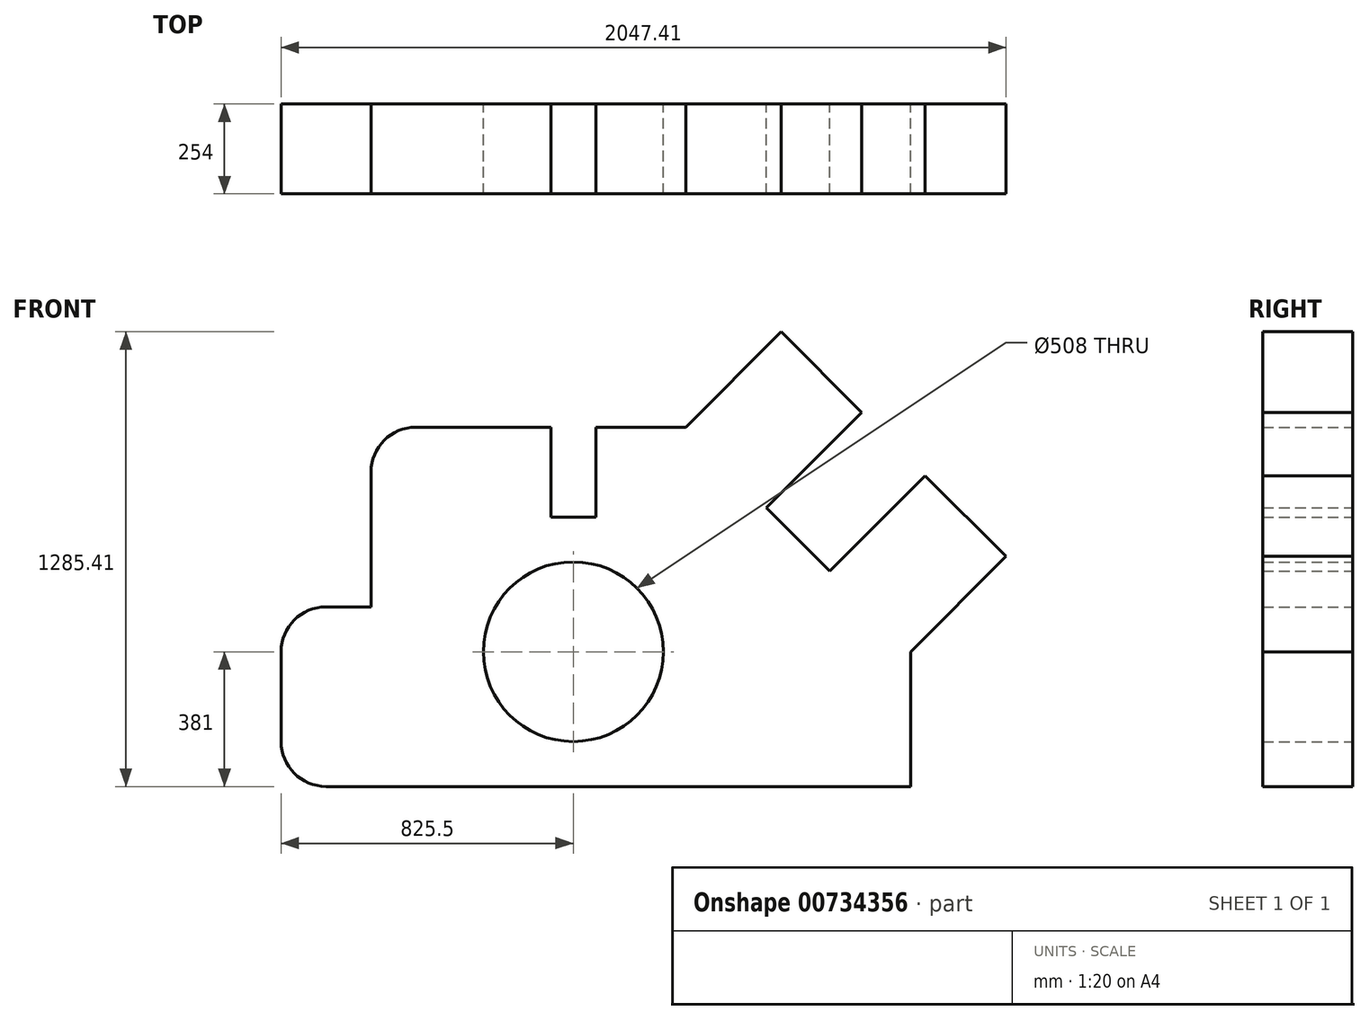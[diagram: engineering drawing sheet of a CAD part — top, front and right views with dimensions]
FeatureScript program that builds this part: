
annotation { "Feature Type Name" : "Feature", "Feature Type Description" : "" }
export const myFeature = defineFeature(function(context is Context, id is Id, definition is map)
    precondition{}
    {
        {
            var Q0;
            Q0=qCreatedBy(makeId("Front.planeOp"),FACE);
            var sketch = newSketch(context, id + "F0", { "sketchPlane" : qUnion([Q0])});
            skLineSegment(sketch, "E0", {"start": v(0, 127) * mm, "end": v(0, 381) * mm});
            skLineSegment(sketch, "E1", {"start": v(127, 0) * mm, "end": v(1778, 0) * mm});
            skLineSegment(sketch, "E2", {"start": v(1778, 0) * mm, "end": v(1778, 381) * mm});
            skLineSegment(sketch, "E3", {"start": v(1778, 381) * mm, "end": v(2047.4, 650.4) * mm});
            skLineSegment(sketch, "E4", {"start": v(127, 508) * mm, "end": v(254, 508) * mm});
            skLineSegment(sketch, "E5", {"start": v(254, 508) * mm, "end": v(254, 889) * mm});
            skLineSegment(sketch, "E6", {"start": v(381, 1016) * mm, "end": v(762, 1016) * mm});
            skLineSegment(sketch, "E7", {"start": v(762, 1016) * mm, "end": v(762, 762) * mm});
            skLineSegment(sketch, "E8", {"start": v(762, 762) * mm, "end": v(889, 762) * mm});
            skLineSegment(sketch, "E9", {"start": v(889, 762) * mm, "end": v(889, 1016) * mm});
            skLineSegment(sketch, "E10", {"start": v(889, 1016) * mm, "end": v(1143, 1016) * mm});
            skLineSegment(sketch, "E11", {"start": v(1143, 1016) * mm, "end": v(1412.4, 1285.4) * mm});
            skLineSegment(sketch, "E12", {"start": v(1412.4, 1285.4) * mm, "end": v(1639.92, 1057.9) * mm});
            skLineSegment(sketch, "E13", {"start": v(1639.92, 1057.9) * mm, "end": v(1370.51, 788.49) * mm});
            skLineSegment(sketch, "E14", {"start": v(1370.51, 788.49) * mm, "end": v(1550.12, 608.88) * mm});
            skLineSegment(sketch, "E15", {"start": v(1550.12, 608.88) * mm, "end": v(1819.53, 878.29) * mm});
            skLineSegment(sketch, "E16", {"start": v(1819.53, 878.29) * mm, "end": v(2047.4, 650.4) * mm});
            skCircle(sketch, "E17", {"center": v(825.5, 381) * mm, "radius": 254 * mm});
            skPoint(sketch, "E18.visualSharp", {"position": v(254, 1016) * mm});
            skArc(sketch, "E18.filletArc", {"start": v(381, 1016) * mm, "mid": v(291.2, 978.8) * mm, "end": v(254, 889) * mm});
            skPoint(sketch, "E19.visualSharp", {"position": v(0, 508) * mm});
            skArc(sketch, "E19.filletArc", {"start": v(127, 508) * mm, "mid": v(37.2, 470.8) * mm, "end": v(0, 381) * mm});
            skPoint(sketch, "E20.visualSharp", {"position": v(0, 0) * mm});
            skArc(sketch, "E20.filletArc", {"start": v(0, 127) * mm, "mid": v(37.2, 37.2) * mm, "end": v(127, 0) * mm});
            skSolve(sketch);
        }
        {
            var Q0;
            Q0=makeQuery(id+"F0.imprint","IMPRINT",FACE,{"disambiguationData":[TD([[makeQuery(id+"F0.imprint","IMPRINT",EDGE,{"derivedFrom":sQuery(id+"F0.wireOp",EDGE,"E0")}),-1.0]])]});
            extrude(context, id + "F1", {"entities" : qUnion([Q0]), "depth" : 254 * mm, "offsetDistance" : 25.4 * mm});
        }
    });
